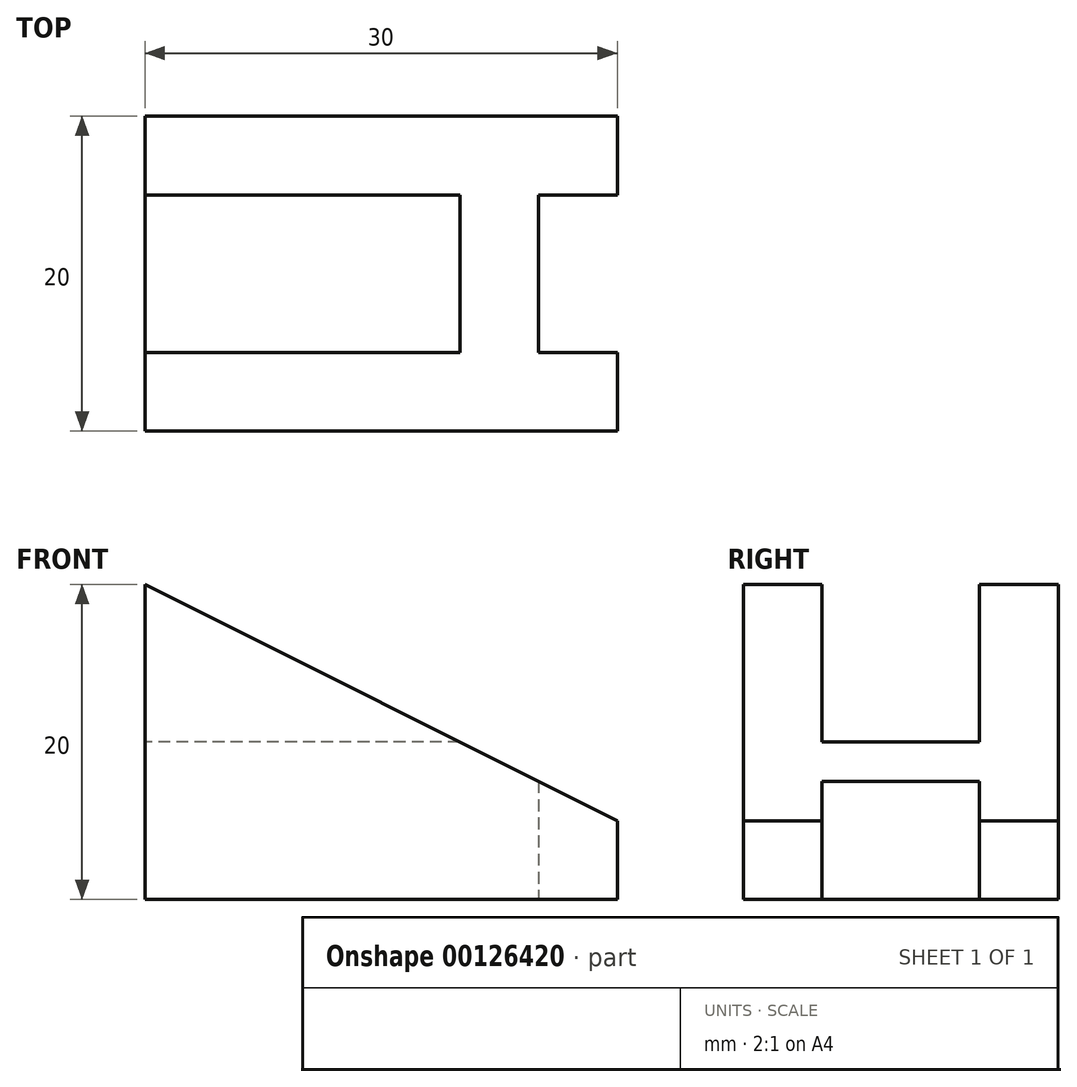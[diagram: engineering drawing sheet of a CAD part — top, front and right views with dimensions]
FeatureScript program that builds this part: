
annotation { "Feature Type Name" : "Feature", "Feature Type Description" : "" }
export const myFeature = defineFeature(function(context is Context, id is Id, definition is map)
    precondition{}
    {
        {
            var Q0;
            Q0=qCreatedBy(makeId("Front.planeOp"),FACE);
            var sketch = newSketch(context, id + "F0", { "sketchPlane" : qUnion([Q0])});
            skLineSegment(sketch, "E0", {"start": v(0, 0) * mm, "end": v(0, 20) * mm});
            skLineSegment(sketch, "E1", {"start": v(0, 20) * mm, "end": v(30, 5) * mm});
            skLineSegment(sketch, "E2", {"start": v(30, 5) * mm, "end": v(30, 0) * mm});
            skLineSegment(sketch, "E3", {"start": v(30, 0) * mm, "end": v(0, 0) * mm});
            skSolve(sketch);
        }
        {
            var Q0;
            Q0=makeQuery(id+"F0.imprint","IMPRINT",FACE,{"disambiguationData":[TD([[makeQuery(id+"F0.imprint","IMPRINT",EDGE,{"derivedFrom":sQuery(id+"F0.wireOp",EDGE,"E0")}),-1.0]])]});
            extrude(context, id + "F1", {"entities" : qUnion([Q0]), "depth" : 20 * mm});
        }
        {
            var Q0;
            Q0=makeQuery(id+"F1.opExtrude","SWEPT_FACE",FACE,{"disambiguationData":[OSD([sQuery(id+"F0.wireOp",EDGE,"E0")])]});
            var sketch = newSketch(context, id + "F2", { "sketchPlane" : qUnion([Q0])});
            skLineSegment(sketch, "E4", {"start": v(0, 20) * mm, "end": v(5, 20) * mm, "construction": true});
            skLineSegment(sketch, "E5", {"start": v(5, 20) * mm, "end": v(15, 20) * mm, "construction": true});
            skLineSegment(sketch, "E6", {"start": v(15, 20) * mm, "end": v(20, 20) * mm, "construction": true});
            skLineSegment(sketch, "E7.bottom", {"start": v(5, 20) * mm, "end": v(15, 20) * mm});
            skLineSegment(sketch, "E7.top", {"start": v(5, 10) * mm, "end": v(15, 10) * mm});
            skLineSegment(sketch, "E7.left", {"start": v(5, 20) * mm, "end": v(5, 10) * mm});
            skLineSegment(sketch, "E7.right", {"start": v(15, 20) * mm, "end": v(15, 10) * mm});
            skSolve(sketch);
        }
        {
            var Q0;
            Q0=makeQuery(id+"F2.imprint","IMPRINT",FACE,{"disambiguationData":[TD([[makeQuery(id+"F2.imprint","IMPRINT",EDGE,{"derivedFrom":sQuery(id+"F2.wireOp",EDGE,"E7.bottom")}),1.0]])]});
            extrude(context, id + "F3", {"entities" : qUnion([Q0]), "operationType" : NewBodyOperationType.REMOVE, "endBound" : BoundingType.THROUGH_ALL, "oppositeDirection" : true, "depth" : 25 * mm});
        }
        {
            var Q0;
            Q0=makeQuery(id+"F1.opExtrude","SWEPT_FACE",FACE,{"disambiguationData":[OSD([sQuery(id+"F0.wireOp",EDGE,"E3")])]});
            var sketch = newSketch(context, id + "F4", { "sketchPlane" : qUnion([Q0])});
            skLineSegment(sketch, "E8", {"start": v(30, 20) * mm, "end": v(30, 15) * mm, "construction": true});
            skLineSegment(sketch, "E9", {"start": v(30, 15) * mm, "end": v(30, 5) * mm, "construction": true});
            skLineSegment(sketch, "E10", {"start": v(30, 5) * mm, "end": v(30, 0) * mm, "construction": true});
            skLineSegment(sketch, "E11.bottom", {"start": v(30, 15) * mm, "end": v(25, 15) * mm});
            skLineSegment(sketch, "E11.top", {"start": v(30, 5) * mm, "end": v(25, 5) * mm});
            skLineSegment(sketch, "E11.left", {"start": v(30, 15) * mm, "end": v(30, 5) * mm});
            skLineSegment(sketch, "E11.right", {"start": v(25, 15) * mm, "end": v(25, 5) * mm});
            skSolve(sketch);
        }
        {
            var Q0;
            Q0=makeQuery(id+"F4.imprint","IMPRINT",FACE,{"disambiguationData":[TD([[makeQuery(id+"F4.imprint","IMPRINT",EDGE,{"derivedFrom":sQuery(id+"F4.wireOp",EDGE,"E11.bottom")}),1.0]])]});
            extrude(context, id + "F5", {"entities" : qUnion([Q0]), "operationType" : NewBodyOperationType.REMOVE, "endBound" : BoundingType.THROUGH_ALL, "oppositeDirection" : true, "depth" : 25 * mm});
        }
    });
